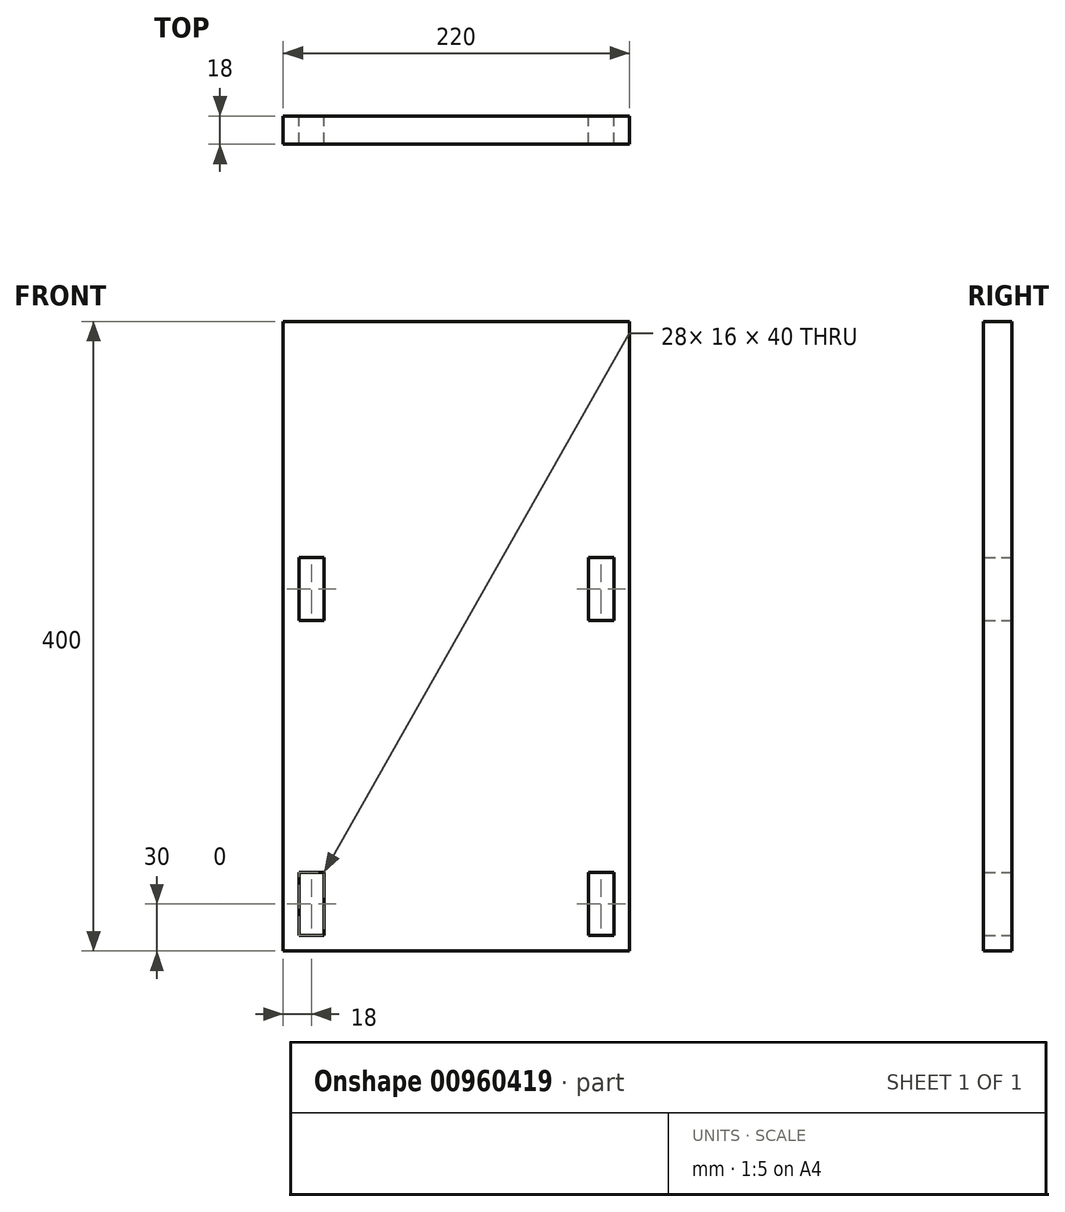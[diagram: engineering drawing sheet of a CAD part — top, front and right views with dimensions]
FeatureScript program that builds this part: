
annotation { "Feature Type Name" : "Feature", "Feature Type Description" : "" }
export const myFeature = defineFeature(function(context is Context, id is Id, definition is map)
    precondition{}
    {
        {
            var Q0;
            Q0=qCreatedBy(makeId("Front.planeOp"),FACE);
            var sketch = newSketch(context, id + "F0", { "sketchPlane" : qUnion([Q0])});
            skLineSegment(sketch, "E0.bottom", {"start": v(110, 200) * mm, "end": v(-110, 200) * mm});
            skLineSegment(sketch, "E0.top", {"start": v(110, -200) * mm, "end": v(-110, -200) * mm});
            skLineSegment(sketch, "E0.left", {"start": v(110, 200) * mm, "end": v(110, -200) * mm});
            skLineSegment(sketch, "E0.right", {"start": v(-110, 200) * mm, "end": v(-110, -200) * mm});
            skPoint(sketch, "E0.middle", {"position": v(0, 0) * mm});
            skLineSegment(sketch, "E1.bottom", {"start": v(100, -190) * mm, "end": v(84, -190) * mm});
            skLineSegment(sketch, "E1.top", {"start": v(100, -150) * mm, "end": v(84, -150) * mm});
            skLineSegment(sketch, "E1.left", {"start": v(100, -190) * mm, "end": v(100, -150) * mm});
            skLineSegment(sketch, "E1.right", {"start": v(84, -190) * mm, "end": v(84, -150) * mm});
            skPoint(sketch, "E1.middle", {"position": v(92, -170) * mm});
            skLineSegment(sketch, "E2.MirrorCS", {"start": v(-84, -190) * mm, "end": v(-84, -150) * mm});
            skLineSegment(sketch, "E3.MirrorCS", {"start": v(-100, -150) * mm, "end": v(-84, -150) * mm});
            skLineSegment(sketch, "E4.MirrorCS", {"start": v(-100, -190) * mm, "end": v(-100, -150) * mm});
            skLineSegment(sketch, "E5.MirrorCS", {"start": v(-100, -190) * mm, "end": v(-84, -190) * mm});
            skLineSegment(sketch, "E6", {"start": v(-114.4, -70) * mm, "end": v(139.2, -70) * mm, "construction": true});
            skLineSegment(sketch, "E7.MirrorCS", {"start": v(100, 10) * mm, "end": v(84, 10) * mm});
            skLineSegment(sketch, "E8.MirrorCS", {"start": v(84, 50) * mm, "end": v(84, 10) * mm});
            skLineSegment(sketch, "E9.MirrorCS", {"start": v(100, 50) * mm, "end": v(100, 10) * mm});
            skLineSegment(sketch, "E10.MirrorCS", {"start": v(100, 50) * mm, "end": v(84, 50) * mm});
            skLineSegment(sketch, "E11.MirrorCS", {"start": v(-84, 50) * mm, "end": v(-84, 10) * mm});
            skLineSegment(sketch, "E12.MirrorCS", {"start": v(-100, 10) * mm, "end": v(-84, 10) * mm});
            skLineSegment(sketch, "E13.MirrorCS", {"start": v(-100, 50) * mm, "end": v(-100, 10) * mm});
            skLineSegment(sketch, "E14.MirrorCS", {"start": v(-100, 50) * mm, "end": v(-84, 50) * mm});
            skSolve(sketch);
        }
        {
            var Q0;
            Q0=makeQuery(id+"F0.imprint","IMPRINT",FACE,{"disambiguationData":[TD([[makeQuery(id+"F0.imprint","IMPRINT",EDGE,{"derivedFrom":sQuery(id+"F0.wireOp",EDGE,"E0.bottom")}),1.0]])]});
            extrude(context, id + "F1", {"entities" : qUnion([Q0]), "depth" : 18 * mm, "offsetDistance" : 25 * mm});
        }
    });
